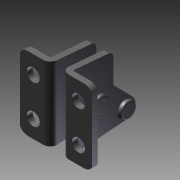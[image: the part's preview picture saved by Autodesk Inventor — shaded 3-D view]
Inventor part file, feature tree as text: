
AUTODESK INVENTOR PART (.ipt)
format: ipt  version: 2011 SP1 (Build 150282100, 282)  size: 208,896 bytes
history: native  units: mm
features: other x14, sketch x10, extrude x8, revolve x2
ambient origin geometry x8: Origin, YZ Plane, XZ Plane, XY Plane, X Axis, Y Axis, Z Axis, Center Point
bodies: Solid1 (feature_tree)
feature tree (34):
  extrude  "Extrusion1"  TaperAngle=360.0deg  [1 undecoded]
  revolve  "Revolution1"  [1 undecoded]
  revolve  "Revolution2"  [1 undecoded]
  extrude  "Extrusion2"  Depth=2.0mm TaperAngle=0.0deg
  extrude  "Extrusion3"  Depth=2.0mm TaperAngle=0.0deg
  extrude  "Extrusion4"  [1 undecoded]
  extrude  "Extrusion5"  [1 undecoded]
  extrude  "Extrusion6"  [1 undecoded]
  extrude  "Extrusion7"  [1 undecoded]
  extrude  "Extrusion8"  [1 undecoded]
  other  "WF1_XY"
  other  "WF1_YZ"
  other  "WF1_ZX"
  other  "WF1_X"
  other  "WF1_Y"
  other  "WF1_Z"
  other  "WF1_Center"
  other  "WF2_XY"
  other  "WF2_YZ"
  other  "WF2_ZX"
  other  "WF2_X"
  other  "WF2_Y"
  other  "WF2_Z"
  other  "WF2_Center"
  sketch  "Skizze_1"  dims[d0=26.0mm d1=0.0mm d2=360.0deg]
  sketch  "Skizze_2"  dims[d6=100.0mm d7=0.0mm d8=2.0mm d9=0.0mm]
  sketch  "Skizze_3"  dims[d14=2.0mm d15=0.0mm d16=2.0mm d17=0.0mm]
  sketch  "Skizze_5"
  sketch  "Skizze_6"
  sketch  "Skizze_7"
  sketch  "Skizze_8_ALT_Drilling_1"  dims[d3=360.0deg d4=26.0mm d5=0.0mm]
  sketch  "Skizze_9_ALT_Drilling_2"  dims[d10=2.0mm d11=0.0mm d12=2.0mm d13=0.0mm]
  sketch  "Skizze_10_ALT_Drilling_3"
  sketch  "Skizze_11_ALT_Drilling_4"
note: 8 required parameter values undecoded (feature->parameter linkage not recoverable at this tier; creation-order binding heuristic only, values carry confidence <= 0.55)